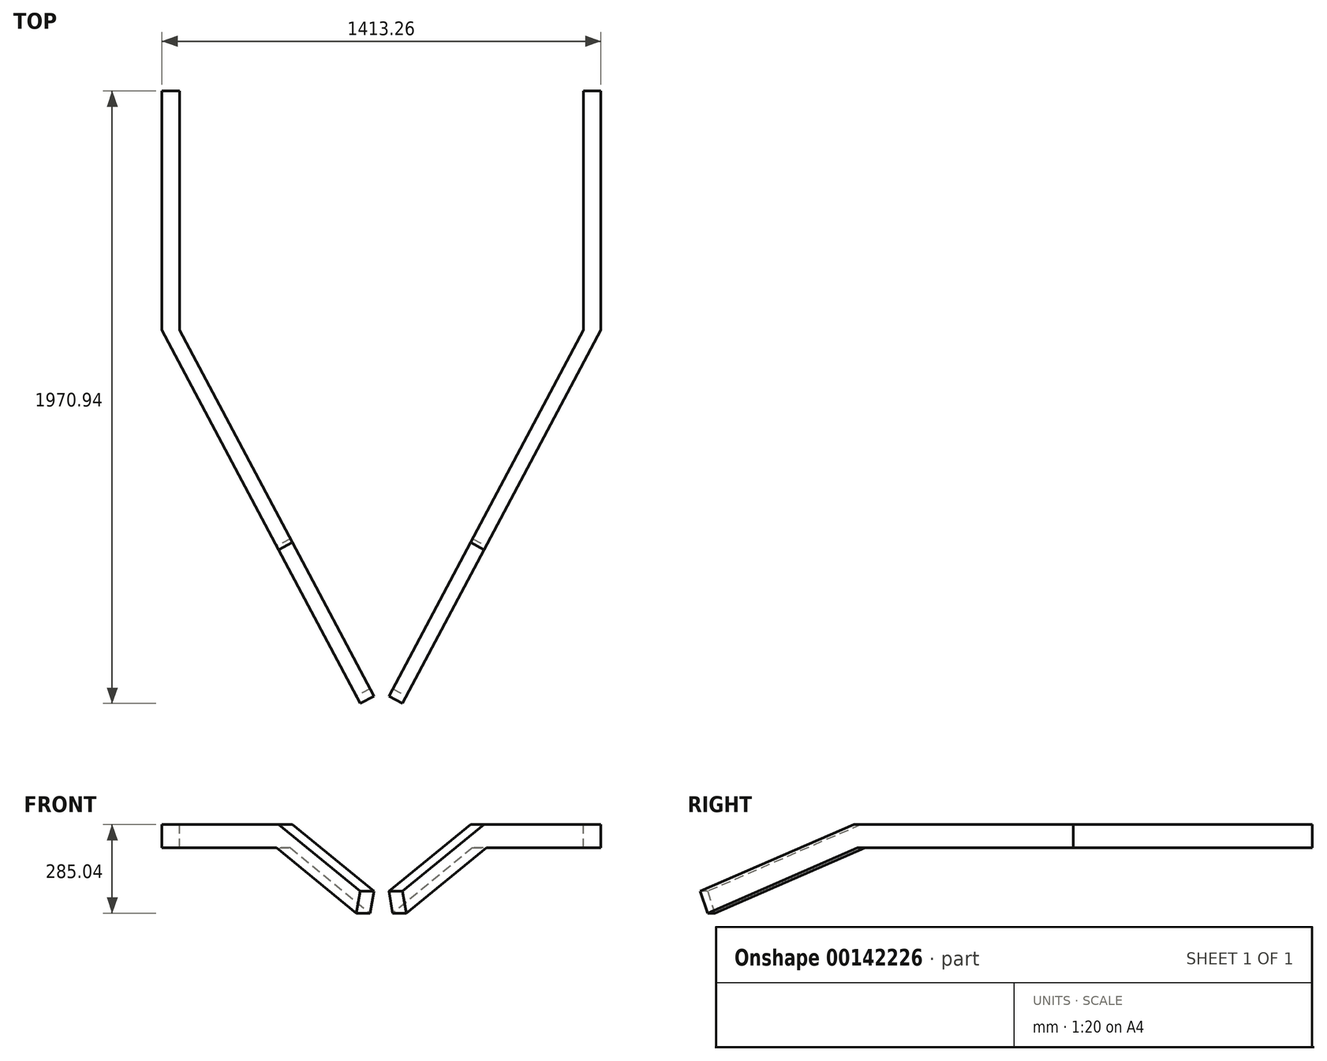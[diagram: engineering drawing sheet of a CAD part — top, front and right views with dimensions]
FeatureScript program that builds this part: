
annotation { "Feature Type Name" : "Feature", "Feature Type Description" : "" }
export const myFeature = defineFeature(function(context is Context, id is Id, definition is map)
    precondition{}
    {
        {
            var Q0;
            Q0=qCreatedBy(makeId("Top.planeOp"),FACE);
            var sketch = newSketch(context, id + "F0", { "sketchPlane" : qUnion([Q0])});
            skLineSegment(sketch, "E0.bottom", {"start": v(650, 0) * mm, "end": v(706.63, 0) * mm});
            skLineSegment(sketch, "E0.left", {"start": v(650, 0) * mm, "end": v(650, -770) * mm});
            skLineSegment(sketch, "E0.right", {"start": v(706.63, 0) * mm, "end": v(706.63, -770) * mm});
            skLineSegment(sketch, "E1", {"start": v(706.63, -770) * mm, "end": v(331.05, -1476.36) * mm});
            skLineSegment(sketch, "E2", {"start": v(650, -770) * mm, "end": v(286.9, -1452.88) * mm});
            skLineSegment(sketch, "E3", {"start": v(331.05, -1476.36) * mm, "end": v(286.9, -1452.88) * mm});
            skSolve(sketch);
        }
        {
            var Q0;
            Q0=makeQuery(id+"F0.imprint","IMPRINT",FACE,{"disambiguationData":[TD([[makeQuery(id+"F0.imprint","IMPRINT",EDGE,{"derivedFrom":sQuery(id+"F0.wireOp",EDGE,"E0.bottom")}),-1.0]])]});
            extrude(context, id + "F1", {"entities" : qUnion([Q0]), "oppositeDirection" : true, "depth" : 75 * mm});
        }
        {
            var Q0;
            Q0=makeQuery(id+"F1.opExtrude","SWEPT_FACE",FACE,{"disambiguationData":[OSD([sQuery(id+"F0.wireOp",EDGE,"E1")])]});
            cPlane(context, id + "F2", {"entities" : qUnion([Q0]), "cplaneType" : CPlaneType.OFFSET, "offset" : 0 * mm, "width" : 150 * mm, "height" : 150 * mm});
        }
        {
            var Q0;
            Q0=qCreatedBy(id+"F2.planeOp",FACE);
            var sketch = newSketch(context, id + "F3", { "sketchPlane" : qUnion([Q0])});
            skPoint(sketch, "E4", {"position": v(-1148.13, 0) * mm});
            skLineSegment(sketch, "E5", {"start": v(-1148.13, 0) * mm, "end": v(-1708.28, -215.02) * mm});
            skLineSegment(sketch, "E6.0", {"start": v(-1148.13, -75) * mm, "end": v(-1148.13, 0) * mm});
            skLineSegment(sketch, "E7.0", {"start": v(-1126.15, -71.9) * mm, "end": v(-1681.4, -285.04) * mm});
            skLineSegment(sketch, "E8", {"start": v(-1148.13, 0) * mm, "end": v(-1126.15, -71.9) * mm});
            skLineSegment(sketch, "E9", {"start": v(-1708.28, -215.02) * mm, "end": v(-1681.4, -285.04) * mm});
            skSolve(sketch);
        }
        {
            var Q0;
            Q0 = qSketchRegion(id + "F3", true);
            extrude(context, id + "F4", {"entities" : qUnion([Q0]), "operationType" : NewBodyOperationType.ADD, "oppositeDirection" : true, "depth" : 50 * mm});
        }
        {
            var Q0;
            Q0=qCreatedBy(makeId("Top.planeOp"),FACE);
            var sketch = newSketch(context, id + "F5", { "sketchPlane" : qUnion([Q0])});
            skLineSegment(sketch, "E10", {"start": v(0, 0) * mm, "end": v(0, -2100.88) * mm});
            skLineSegment(sketch, "E11.0", {"start": v(45, 0) * mm, "end": v(45, -2100.88) * mm});
            skSolve(sketch);
        }
        {
            var Q0;
            Q0=makeQuery(id+"F1.opExtrude","SWEPT_BODY",BODY,{"disambiguationData":[OSD([sQuery(id+"F0.wireOp",EDGE,"E0.bottom"),sQuery(id+"F0.wireOp",EDGE,"E0.left"),sQuery(id+"F0.wireOp",EDGE,"E0.right"),sQuery(id+"F0.wireOp",EDGE,"E1"),sQuery(id+"F0.wireOp",EDGE,"E2"),sQuery(id+"F0.wireOp",EDGE,"E3")])]});
            var Q1;
            Q1=qCreatedBy(makeId("Right.planeOp"),FACE);
            mirror(context, id + "F6", {"entities" : qUnion([Q0]), "mirrorPlane" : qUnion([Q1])});
        }
    });
